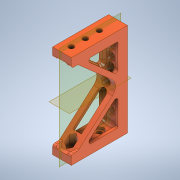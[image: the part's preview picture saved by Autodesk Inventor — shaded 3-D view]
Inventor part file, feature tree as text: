
AUTODESK INVENTOR PART (.ipt)
format: ipt  version: 2020 (Build 240168000, 168)  size: 619,520 bytes
history: native  units: in
note: dims shown in document units (in); Inventor stores cm internally (conversion verified against a paired STEP export)
features: extrude x14, sketch x12, projected_geometry x7, plane x5, fillet x4, chamfer x2, mirror x1
ambient origin geometry x8: Origin, YZ Plane, XZ Plane, XY Plane, X Axis, Y Axis, Z Axis, Center Point
bodies: Solid1 (feature_tree)
feature tree (45):
  extrude  "Extrusion1"  Depth=1.0in
  extrude  "Extrusion2"  Depth=0.5in
  fillet  "Fillet1"  Radius=0.5in
  extrude  "Extrusion3"  Depth=0.25in
  fillet  "Fillet2"  Radius=0.25in
  extrude  "Extrusion4"  Depth=0.5in
  plane  "Work Plane1"
  extrude  "Extrusion5"  Depth=2.5in
  extrude  "Extrusion6"  TaperAngle=0.0deg  [1 undecoded]
  plane  "Work Plane2"
  extrude  "Extrusion7"  Depth=0.4532in
  plane  "Work Plane3"
  extrude  "Extrusion8"  Depth=0.25in TaperAngle=0.0deg
  extrude  "Extrusion10"  Depth=0.5in
  plane  "Work Plane4"
  plane  "Work Plane5"
  extrude  "Extrusion11"  Depth=0.3937in
  chamfer  "Chamfer1"  [1 undecoded]
  extrude  "Extrusion12"  Depth=0.4532in
  extrude  "Extrusion13"  [1 undecoded]
  chamfer  "Chamfer2"  Distance=0.4532in
  fillet  "Fillet3"  Radius=2.5in
  fillet  "Fillet4"  Radius=0.375in
  extrude  "Extrusion14"  Depth=1.0in TaperAngle=0.0deg
  extrude  "Extrusion15"  [1 undecoded]
  mirror  "Mirror2"
  sketch  "Sketch1"  dims[d0=1.0in d1=5.0in]
  sketch  "Sketch2"  dims[d2=3.0in d3=0.0in d4=0.5in d5=0.5in]
  sketch  "Sketch3"  dims[d6=0.0in d7=0.0in d8=0.05in d9=0.25in]
  sketch  "Sketch4"  dims[d10=1.0in d11=0.0in d12=0.5in d13=0.125in]
  sketch  "Sketch6"  dims[d14=0.2in d16=2.5in]
  sketch  "Sketch8"  dims[d17=4.3307in d19=0.5in d20=0.3937in d22=1.0in d24=0.0in d25=0.0in]
  sketch  "Sketch10"  dims[d26=-0.25in d27=0.4532in]
  sketch  "Sketch11"  dims[d28=3.5433in d30=0.5in d31=0.3937in d33=1.0in d35=0.25in d36=0.0in]
  sketch  "Sketch12"  dims[d37=1.0in d38=0.5in]
  projected_geometry  "Projected Loop1"
  projected_geometry  "Projected Loop2"
  projected_geometry  "Projected Loop3"
  sketch  "Sketch13"  dims[d39=0.2656in d40=1.1811in d42=0.75in d43=0.3937in d45=1.0in d47=0.0in d48=0.0in]
  projected_geometry  "Projected Loop4"
  projected_geometry  "Projected Loop5"
  projected_geometry  "Projected Loop6"
  sketch  "Sketch14"  dims[d49=-0.25in d50=0.4532in]
  sketch  "Sketch15"  dims[d51=2.5in d52=0.0in d53=-0.25in d54=0.4532in d55=2.5in d56=0.0in d59=0.375in d60=0.26in d61=0.0in d62=-0.5in d63=0.375in d64=0.375in d65=0.375in d66=0.4532in d67=0.0in d68=0.125in d69=0.125in d70=45.0deg d71=0.4532in d72=0.0in d73=0.975in d74=0.0in d75=0.125in d76=0.125in d77=45.0deg d78=0.125in d79=0.175in d80=1.0in d81=0.0in d82=1.0in d83=0.0in]
  projected_geometry  "Projected Loop7"
note: 4 required parameter values undecoded (feature->parameter linkage not recoverable at this tier; creation-order binding heuristic only, values carry confidence <= 0.55)
